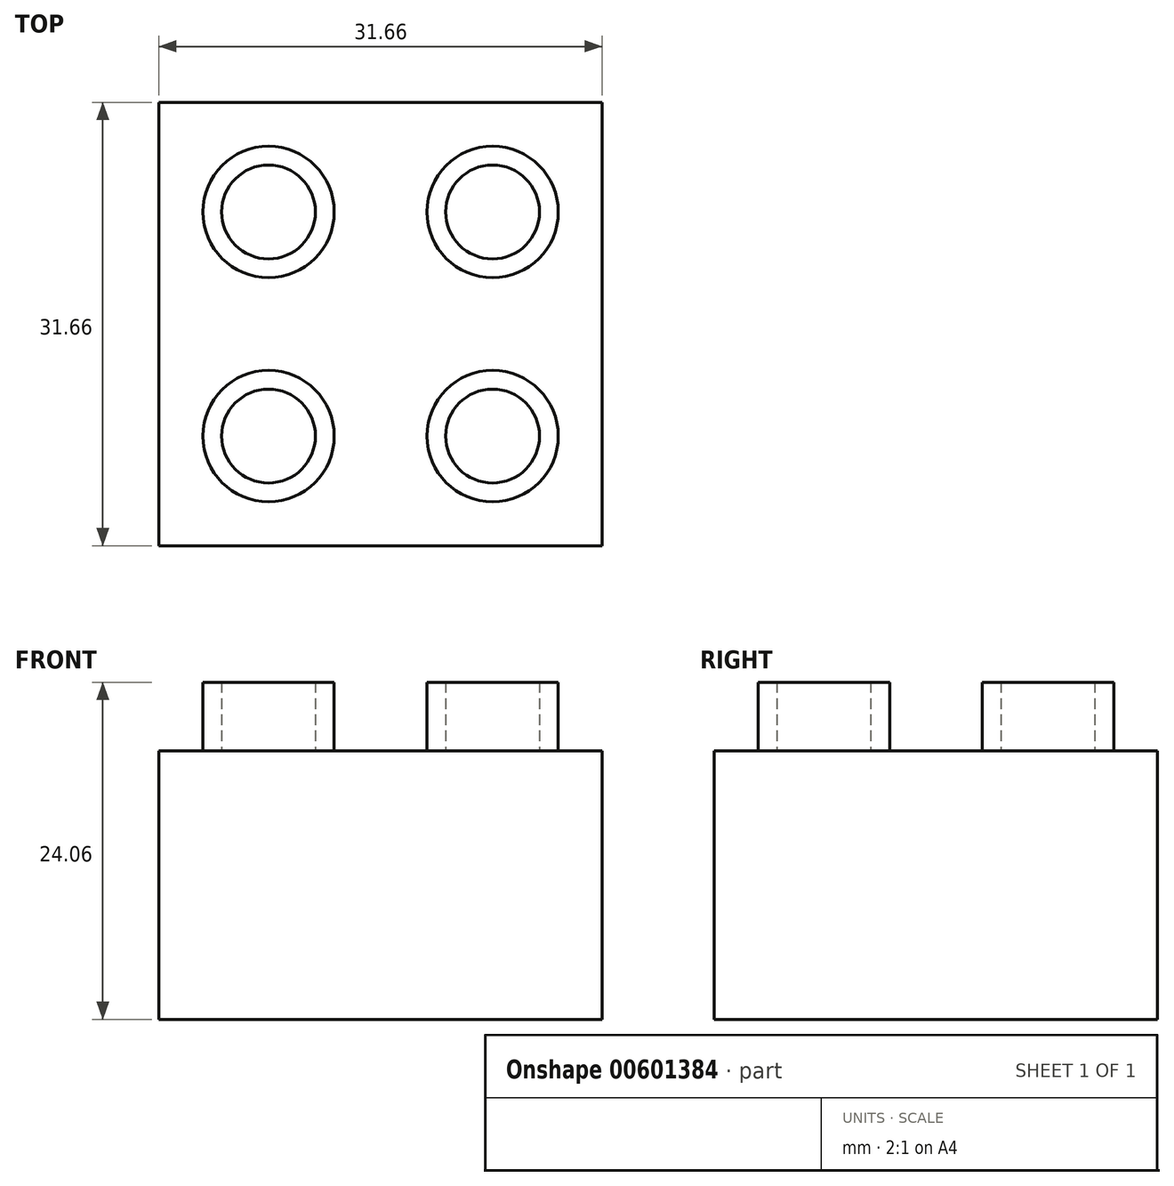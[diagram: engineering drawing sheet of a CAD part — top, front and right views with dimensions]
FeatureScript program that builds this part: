
annotation { "Feature Type Name" : "Feature", "Feature Type Description" : "" }
export const myFeature = defineFeature(function(context is Context, id is Id, definition is map)
    precondition{}
    {
        {
            var Q0;
            Q0=qCreatedBy(makeId("Top.planeOp"),FACE);
            var sketch = newSketch(context, id + "F0", { "sketchPlane" : qUnion([Q0])});
            skLineSegment(sketch, "E0.bottom", {"start": v(-15.83, 15.83) * mm, "end": v(15.83, 15.83) * mm});
            skLineSegment(sketch, "E0.top", {"start": v(-15.83, -15.83) * mm, "end": v(15.83, -15.83) * mm});
            skLineSegment(sketch, "E0.left", {"start": v(-15.83, 15.83) * mm, "end": v(-15.83, -15.83) * mm});
            skLineSegment(sketch, "E0.right", {"start": v(15.83, 15.83) * mm, "end": v(15.83, -15.83) * mm});
            skSolve(sketch);
        }
        {
            var Q0;
            Q0 = qSketchRegion(id + "F0", true);
            extrude(context, id + "F1", {"entities" : qUnion([Q0]), "depth" : 19.18 * mm, "offsetDistance" : 25 * mm});
        }
        {
            var Q0;
            Q0=makeQuery(id+"F1.opExtrude","CAP_FACE",FACE,{"disambiguationData":[OSD([sQuery(id+"F0.wireOp",EDGE,"E0.bottom"),sQuery(id+"F0.wireOp",EDGE,"E0.top"),sQuery(id+"F0.wireOp",EDGE,"E0.left"),sQuery(id+"F0.wireOp",EDGE,"E0.right")])],"isStart":false});
            var sketch = newSketch(context, id + "F2", { "sketchPlane" : qUnion([Q0])});
            skCircle(sketch, "E1", {"center": v(8, 8) * mm, "radius": 4.7 * mm});
            skCircle(sketch, "E2", {"center": v(8, 8) * mm, "radius": 3.35 * mm});
            skCircle(sketch, "E3.1.0", {"center": v(-8, 8) * mm, "radius": 4.7 * mm});
            skCircle(sketch, "E3.1.1", {"center": v(-8, 8) * mm, "radius": 3.35 * mm});
            skCircle(sketch, "E3.2.0", {"center": v(-8, -8) * mm, "radius": 4.7 * mm});
            skCircle(sketch, "E3.2.1", {"center": v(-8, -8) * mm, "radius": 3.35 * mm});
            skCircle(sketch, "E3.3.0", {"center": v(8, -8) * mm, "radius": 4.7 * mm});
            skCircle(sketch, "E3.3.1", {"center": v(8, -8) * mm, "radius": 3.35 * mm});
            skPoint(sketch, "E3.center", {"position": v(0, 0) * mm});
            skSolve(sketch);
        }
        {
            var Q0;
            Q0 = qSketchRegion(id + "F2", true);
            extrude(context, id + "F3", {"entities" : qUnion([Q0]), "operationType" : NewBodyOperationType.ADD, "depth" : 4.88 * mm, "offsetDistance" : 25 * mm});
        }
    });
